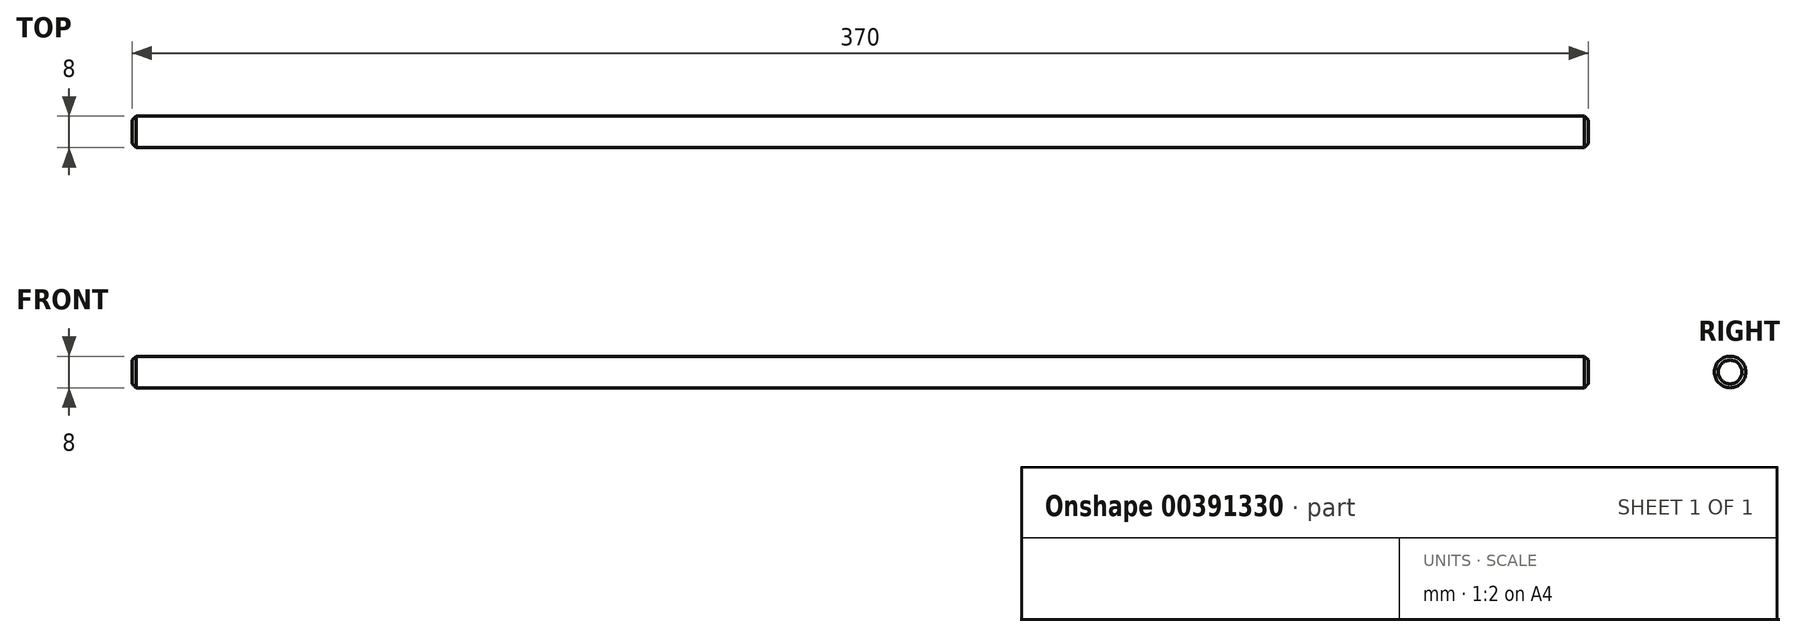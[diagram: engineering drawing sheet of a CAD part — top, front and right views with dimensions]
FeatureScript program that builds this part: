
annotation { "Feature Type Name" : "Feature", "Feature Type Description" : "" }
export const myFeature = defineFeature(function(context is Context, id is Id, definition is map)
    precondition{}
    {
        {
            var Q0;
            Q0=qCreatedBy(makeId("Right.planeOp"),FACE);
            var sketch = newSketch(context, id + "F0", { "sketchPlane" : qUnion([Q0])});
            skCircle(sketch, "E0", {"center": v(0, 0) * mm, "radius": 4 * mm});
            skSolve(sketch);
        }
        {
            var Q0;
            Q0=qSketchRegion(id+"F0",true);
            extrude(context, id + "F1", {"entities" : qUnion([Q0]), "endBound" : BoundingType.SYMMETRIC, "depth" : 370 * mm});
        }
        {
            var Q0;
            Q0=makeQuery(id+"F1.opExtrude","CAP_EDGE",EDGE,{"disambiguationData":[OSD([sQuery(id+"F0.wireOp",EDGE,"E0")])],"isStart":false});
            var Q1;
            Q1=makeQuery(id+"F1.opExtrude","CAP_EDGE",EDGE,{"disambiguationData":[OSD([sQuery(id+"F0.wireOp",EDGE,"E0")])],"isStart":true});
            chamfer(context, id + "F2", {"entities" : qUnion([Q0, Q1]), "width" : 1 * mm, "tangentPropagation" : true});
        }
    });
